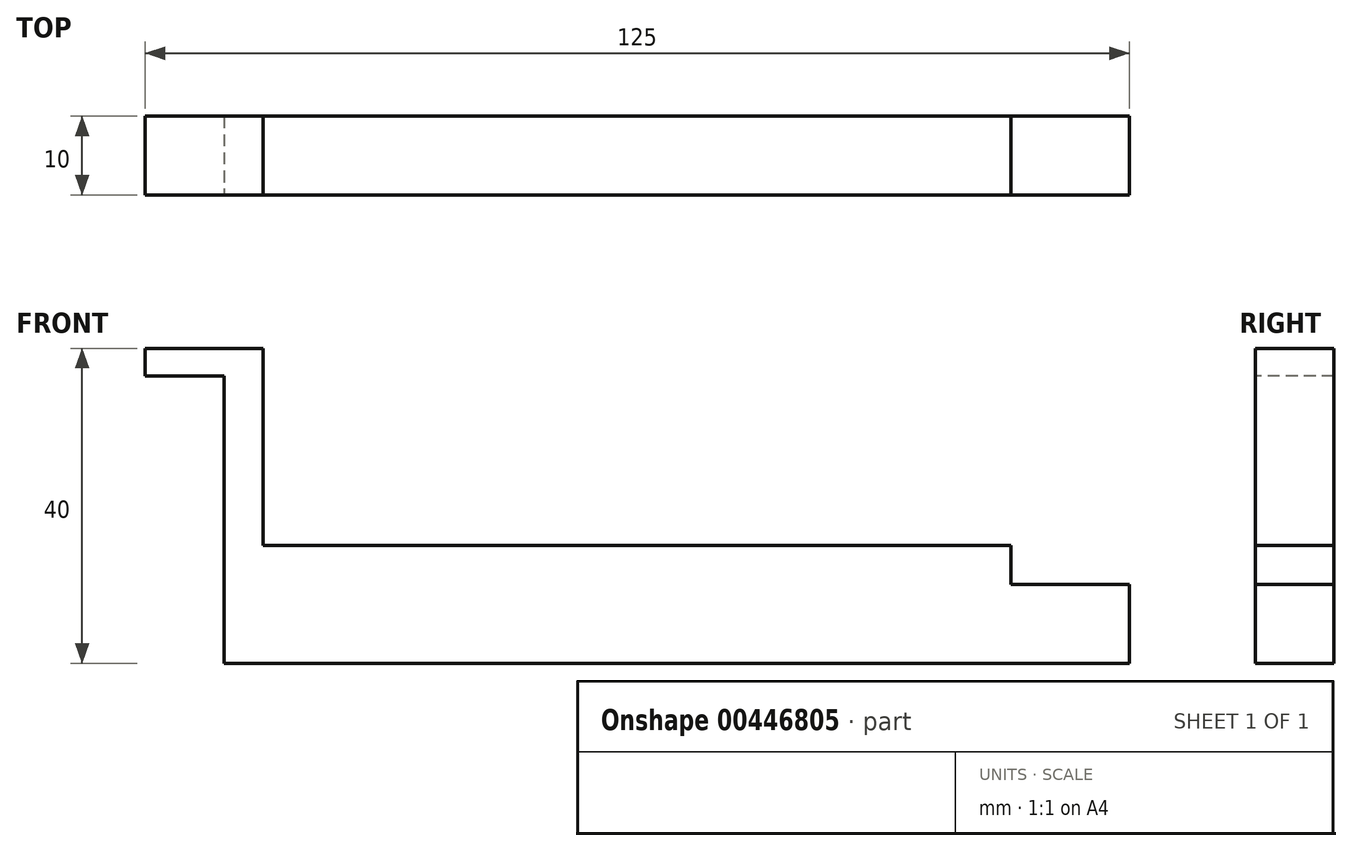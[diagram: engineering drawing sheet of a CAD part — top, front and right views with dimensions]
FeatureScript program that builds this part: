
annotation { "Feature Type Name" : "Feature", "Feature Type Description" : "" }
export const myFeature = defineFeature(function(context is Context, id is Id, definition is map)
    precondition{}
    {
        {
            var Q0;
            Q0=qCreatedBy(makeId("Front.planeOp"),FACE);
            var sketch = newSketch(context, id + "F0", { "sketchPlane" : qUnion([Q0])});
            skLineSegment(sketch, "E0.bottom", {"start": v(-57.5, 7.5) * mm, "end": v(57.5, 7.5) * mm});
            skLineSegment(sketch, "E0.top", {"start": v(-57.5, -7.5) * mm, "end": v(57.5, -7.5) * mm});
            skLineSegment(sketch, "E0.left", {"start": v(-57.5, 7.5) * mm, "end": v(-57.5, -7.5) * mm});
            skLineSegment(sketch, "E0.right", {"start": v(57.5, 7.5) * mm, "end": v(57.5, -7.5) * mm});
            skSolve(sketch);
        }
        {
            var Q0;
            Q0=qSketchRegion(id+"F0",true);
            extrude(context, id + "F1", {"entities" : qUnion([Q0]), "depth" : 10 * mm});
        }
        {
            var Q0;
            Q0=makeQuery(id+"F1.opExtrude","SWEPT_FACE",FACE,{"disambiguationData":[OSD([sQuery(id+"F0.wireOp",EDGE,"E0.bottom")])]});
            var sketch = newSketch(context, id + "F2", { "sketchPlane" : qUnion([Q0])});
            skLineSegment(sketch, "E1.bottom", {"start": v(57.5, 0) * mm, "end": v(42.5, 0) * mm});
            skLineSegment(sketch, "E1.top", {"start": v(57.5, -10) * mm, "end": v(42.5, -10) * mm});
            skLineSegment(sketch, "E1.left", {"start": v(57.5, 0) * mm, "end": v(57.5, -10) * mm});
            skLineSegment(sketch, "E1.right", {"start": v(42.5, 0) * mm, "end": v(42.5, -10) * mm});
            skSolve(sketch);
        }
        {
            var Q0;
            Q0=makeQuery(id+"F2.imprint","IMPRINT",FACE,{"disambiguationData":[TD([[makeQuery(id+"F2.imprint","IMPRINT",EDGE,{"derivedFrom":sQuery(id+"F2.wireOp",EDGE,"E1.bottom")}),-1.0]])]});
            extrude(context, id + "F3", {"entities" : qUnion([Q0]), "operationType" : NewBodyOperationType.REMOVE, "oppositeDirection" : true, "depth" : 5 * mm});
        }
        {
            var Q0;
            Q0=makeQuery(id+"F1.opExtrude","SWEPT_FACE",FACE,{"disambiguationData":[OSD([sQuery(id+"F0.wireOp",EDGE,"E0.bottom")])]});
            var sketch = newSketch(context, id + "F4", { "sketchPlane" : qUnion([Q0])});
            skLineSegment(sketch, "E2.bottom", {"start": v(-52.5, 0) * mm, "end": v(-57.5, 0) * mm});
            skLineSegment(sketch, "E2.top", {"start": v(-52.5, -10) * mm, "end": v(-57.5, -10) * mm});
            skLineSegment(sketch, "E2.left", {"start": v(-52.5, 0) * mm, "end": v(-52.5, -10) * mm});
            skLineSegment(sketch, "E2.right", {"start": v(-57.5, 0) * mm, "end": v(-57.5, -10) * mm});
            skSolve(sketch);
        }
        {
            var Q0;
            Q0=makeQuery(id+"F4.imprint","IMPRINT",FACE,{"disambiguationData":[TD([[makeQuery(id+"F4.imprint","IMPRINT",EDGE,{"derivedFrom":sQuery(id+"F4.wireOp",EDGE,"E2.bottom")}),-1.0]])]});
            extrude(context, id + "F5", {"entities" : qUnion([Q0]), "operationType" : NewBodyOperationType.ADD, "depth" : 25 * mm});
        }
        {
            var Q0;
            Q0=makeQuery(id+"F5.boolean.opBoolean","MERGE",FACE,{"derivedFrom":[makeQuery(id+"F1.opExtrude","SWEPT_FACE",FACE,{"disambiguationData":[OSD([sQuery(id+"F0.wireOp",EDGE,"E0.left")])]}),makeQuery(id+"F5.opExtrude","SWEPT_FACE",FACE,{"disambiguationData":[OSD([sQuery(id+"F4.wireOp",EDGE,"E2.right")])]})]});
            var sketch = newSketch(context, id + "F6", { "sketchPlane" : qUnion([Q0])});
            skLineSegment(sketch, "E3.bottom", {"start": v(0, 32.5) * mm, "end": v(10, 32.5) * mm});
            skLineSegment(sketch, "E3.top", {"start": v(0, 29) * mm, "end": v(10, 29) * mm});
            skLineSegment(sketch, "E3.left", {"start": v(0, 32.5) * mm, "end": v(0, 29) * mm});
            skLineSegment(sketch, "E3.right", {"start": v(10, 32.5) * mm, "end": v(10, 29) * mm});
            skSolve(sketch);
        }
        {
            var Q0;
            Q0=makeQuery(id+"F6.imprint","IMPRINT",FACE,{"disambiguationData":[TD([[makeQuery(id+"F6.imprint","IMPRINT",EDGE,{"derivedFrom":sQuery(id+"F6.wireOp",EDGE,"E3.bottom")}),1.0]])]});
            extrude(context, id + "F7", {"entities" : qUnion([Q0]), "operationType" : NewBodyOperationType.ADD, "depth" : 10 * mm});
        }
    });
